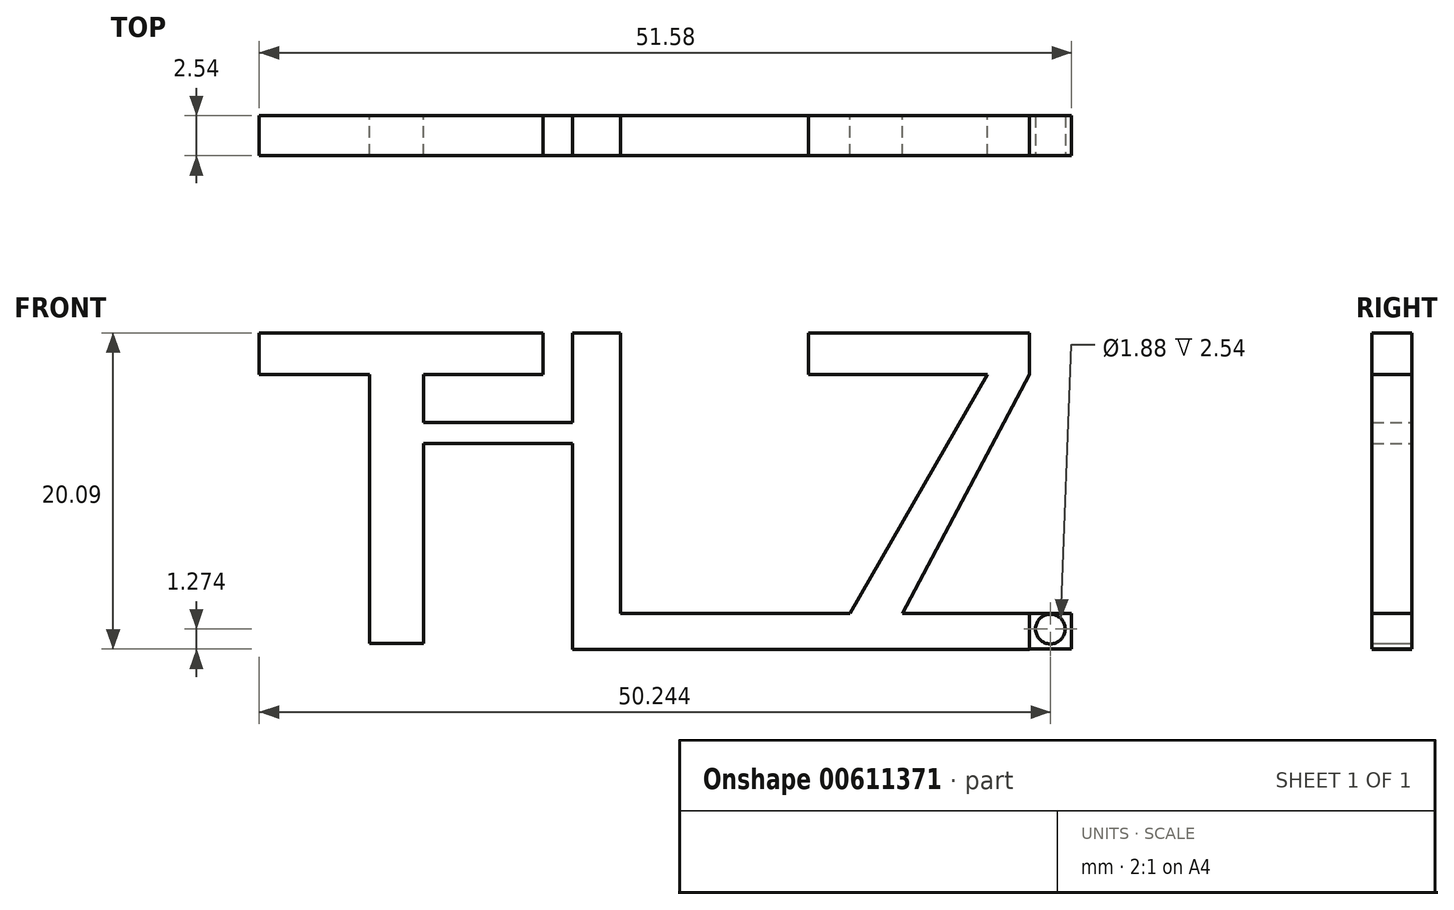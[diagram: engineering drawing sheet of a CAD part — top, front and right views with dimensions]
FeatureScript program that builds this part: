
annotation { "Feature Type Name" : "Feature", "Feature Type Description" : "" }
export const myFeature = defineFeature(function(context is Context, id is Id, definition is map)
    precondition{}
    {
        {
            var Q0;
            Q0=qCreatedBy(makeId("Front.planeOp"),FACE);
            var sketch = newSketch(context, id + "F0", { "sketchPlane" : qUnion([Q0])});
            skLineSegment(sketch, "E0.bottom", {"start": v(-52.04, 33.46) * mm, "end": v(-34.03, 33.46) * mm});
            skLineSegment(sketch, "E0.top", {"start": v(-52.04, 30.8) * mm, "end": v(-34.03, 30.8) * mm});
            skLineSegment(sketch, "E0.left", {"start": v(-52.04, 33.46) * mm, "end": v(-52.04, 30.8) * mm});
            skLineSegment(sketch, "E0.right", {"start": v(-34.03, 33.46) * mm, "end": v(-34.03, 30.8) * mm});
            skLineSegment(sketch, "E1.bottom", {"start": v(-45.03, 30.8) * mm, "end": v(-41.62, 30.8) * mm});
            skLineSegment(sketch, "E1.top", {"start": v(-45.03, 13.75) * mm, "end": v(-41.62, 13.75) * mm});
            skLineSegment(sketch, "E1.left", {"start": v(-45.03, 30.8) * mm, "end": v(-45.03, 13.75) * mm});
            skLineSegment(sketch, "E1.right", {"start": v(-41.62, 30.8) * mm, "end": v(-41.62, 13.75) * mm});
            skLineSegment(sketch, "E2.left", {"start": v(-41.62, 27.78) * mm, "end": v(-41.62, 26.45) * mm});
            skLineSegment(sketch, "E2.right", {"start": v(-32.14, 27.78) * mm, "end": v(-32.14, 26.45) * mm});
            skLineSegment(sketch, "E3.bottom", {"start": v(-32.14, 33.46) * mm, "end": v(-29.1, 33.46) * mm});
            skLineSegment(sketch, "E3.top", {"start": v(-32.14, 13.37) * mm, "end": v(-29.1, 13.37) * mm});
            skLineSegment(sketch, "E3.left", {"start": v(-32.14, 33.46) * mm, "end": v(-32.14, 13.37) * mm});
            skLineSegment(sketch, "E3.right", {"start": v(-29.1, 33.46) * mm, "end": v(-29.1, 13.37) * mm});
            skLineSegment(sketch, "E4.bottom", {"start": v(-29.1, 13.37) * mm, "end": v(-18.1, 13.37) * mm});
            skLineSegment(sketch, "E4.top", {"start": v(-29.1, 15.64) * mm, "end": v(-18.1, 15.64) * mm});
            skLineSegment(sketch, "E4.left", {"start": v(-29.1, 13.37) * mm, "end": v(-29.1, 15.64) * mm});
            skLineSegment(sketch, "E4.right", {"start": v(-18.1, 13.37) * mm, "end": v(-18.1, 15.64) * mm});
            skLineSegment(sketch, "E5.left", {"start": v(-29.1, 33.46) * mm, "end": v(-29.1, 31.95) * mm});
            skLineSegment(sketch, "E5.right", {"start": v(-17.16, 33.46) * mm, "end": v(-17.16, 31.95) * mm});
            skLineSegment(sketch, "E6.bottom", {"start": v(-17.16, 33.46) * mm, "end": v(-3.13, 33.46) * mm});
            skLineSegment(sketch, "E6.top", {"start": v(-17.16, 30.8) * mm, "end": v(-3.13, 30.8) * mm});
            skLineSegment(sketch, "E6.left", {"start": v(-17.16, 33.46) * mm, "end": v(-17.16, 30.8) * mm});
            skLineSegment(sketch, "E6.right", {"start": v(-3.13, 33.46) * mm, "end": v(-3.13, 30.8) * mm});
            skLineSegment(sketch, "E7", {"start": v(-5.78, 30.8) * mm, "end": v(-15.83, 13.37) * mm});
            skLineSegment(sketch, "E8", {"start": v(-15.83, 13.37) * mm, "end": v(-12.42, 13.37) * mm});
            skLineSegment(sketch, "E9", {"start": v(-12.42, 13.37) * mm, "end": v(-3.13, 30.8) * mm});
            skLineSegment(sketch, "E10", {"start": v(-12.42, 13.37) * mm, "end": v(-3.13, 13.37) * mm});
            skLineSegment(sketch, "E11", {"start": v(-3.13, 13.37) * mm, "end": v(-3.13, 15.64) * mm});
            skLineSegment(sketch, "E12", {"start": v(-3.13, 15.64) * mm, "end": v(-11.2, 15.64) * mm});
            skLineSegment(sketch, "E13.bottom", {"start": v(-41.62, 26.45) * mm, "end": v(-32.14, 26.45) * mm});
            skLineSegment(sketch, "E13.top", {"start": v(-41.62, 27.78) * mm, "end": v(-32.14, 27.78) * mm});
            skLineSegment(sketch, "E13.left", {"start": v(-41.62, 26.45) * mm, "end": v(-41.62, 27.78) * mm});
            skLineSegment(sketch, "E13.right", {"start": v(-32.14, 26.45) * mm, "end": v(-32.14, 27.78) * mm});
            skLineSegment(sketch, "E14.bottom", {"start": v(-18.1, 15.64) * mm, "end": v(-12.42, 15.64) * mm});
            skLineSegment(sketch, "E14.top", {"start": v(-18.1, 13.37) * mm, "end": v(-12.42, 13.37) * mm});
            skLineSegment(sketch, "E14.left", {"start": v(-18.1, 15.64) * mm, "end": v(-18.1, 13.37) * mm});
            skLineSegment(sketch, "E14.right", {"start": v(-12.42, 15.64) * mm, "end": v(-12.42, 13.37) * mm});
            skSolve(sketch);
        }
        {
            var Q0;
            Q0 = qSketchRegion(id + "F0", true);
            extrude(context, id + "F1", {"entities" : qUnion([Q0]), "depth" : 2.54 * mm, "offsetDistance" : 25.4 * mm});
        }
        {
            var Q0;
            Q0=makeQuery(id+"F1.opExtrude","CAP_FACE",FACE,{"disambiguationData":[OSD([sQuery(id+"F0.wireOp",EDGE,"E0.bottom"),sQuery(id+"F0.wireOp",EDGE,"E0.top"),sQuery(id+"F0.wireOp",EDGE,"E0.left"),sQuery(id+"F0.wireOp",EDGE,"E0.right"),sQuery(id+"F0.wireOp",EDGE,"E1.top"),sQuery(id+"F0.wireOp",EDGE,"E1.left"),sQuery(id+"F0.wireOp",EDGE,"E1.right"),sQuery(id+"F0.wireOp",EDGE,"E3.bottom"),sQuery(id+"F0.wireOp",EDGE,"E3.top"),sQuery(id+"F0.wireOp",EDGE,"E3.left"),sQuery(id+"F0.wireOp",EDGE,"E3.right"),sQuery(id+"F0.wireOp",EDGE,"E4.bottom"),sQuery(id+"F0.wireOp",EDGE,"E4.top"),sQuery(id+"F0.wireOp",EDGE,"E5.left"),sQuery(id+"F0.wireOp",EDGE,"E6.bottom"),sQuery(id+"F0.wireOp",EDGE,"E6.top"),sQuery(id+"F0.wireOp",EDGE,"E6.left"),sQuery(id+"F0.wireOp",EDGE,"E6.right"),sQuery(id+"F0.wireOp",EDGE,"E7"),sQuery(id+"F0.wireOp",EDGE,"E9"),sQuery(id+"F0.wireOp",EDGE,"E10"),sQuery(id+"F0.wireOp",EDGE,"E11"),sQuery(id+"F0.wireOp",EDGE,"E12"),sQuery(id+"F0.wireOp",EDGE,"E13.bottom"),sQuery(id+"F0.wireOp",EDGE,"E13.top"),sQuery(id+"F0.wireOp",EDGE,"E14.bottom"),sQuery(id+"F0.wireOp",EDGE,"E14.top")])],"isStart":false});
            var sketch = newSketch(context, id + "F2", { "sketchPlane" : qUnion([Q0])});
            skLineSegment(sketch, "E15.bottom", {"start": v(-3.13, 15.64) * mm, "end": v(-0.46, 15.64) * mm});
            skLineSegment(sketch, "E15.top", {"start": v(-3.13, 13.39) * mm, "end": v(-0.46, 13.39) * mm});
            skLineSegment(sketch, "E15.left", {"start": v(-3.13, 15.64) * mm, "end": v(-3.13, 13.39) * mm});
            skLineSegment(sketch, "E15.right", {"start": v(-0.46, 15.64) * mm, "end": v(-0.46, 13.39) * mm});
            skSolve(sketch);
        }
        {
            var Q0;
            Q0 = qSketchRegion(id + "F2", true);
            extrude(context, id + "F3", {"entities" : qUnion([Q0]), "oppositeDirection" : true, "depth" : 2.54 * mm, "offsetDistance" : 25.4 * mm});
        }
        {
            var Q0;
            Q0=makeQuery(id+"F3.opExtrude","CAP_FACE",FACE,{"disambiguationData":[OSD([sQuery(id+"F2.wireOp",EDGE,"E15.bottom"),sQuery(id+"F2.wireOp",EDGE,"E15.top"),sQuery(id+"F2.wireOp",EDGE,"E15.left"),sQuery(id+"F2.wireOp",EDGE,"E15.right")])],"isStart":true});
            var sketch = newSketch(context, id + "F4", { "sketchPlane" : qUnion([Q0])});
            skCircle(sketch, "E16", {"center": v(-1.8, 14.64) * mm, "radius": 0.94 * mm});
            skSolve(sketch);
        }
        {
            var Q0;
            Q0 = qSketchRegion(id + "F4", true);
            extrude(context, id + "F5", {"entities" : qUnion([Q0]), "operationType" : NewBodyOperationType.REMOVE, "oppositeDirection" : true, "depth" : 25.4 * mm, "offsetDistance" : 25.4 * mm});
        }
    });
